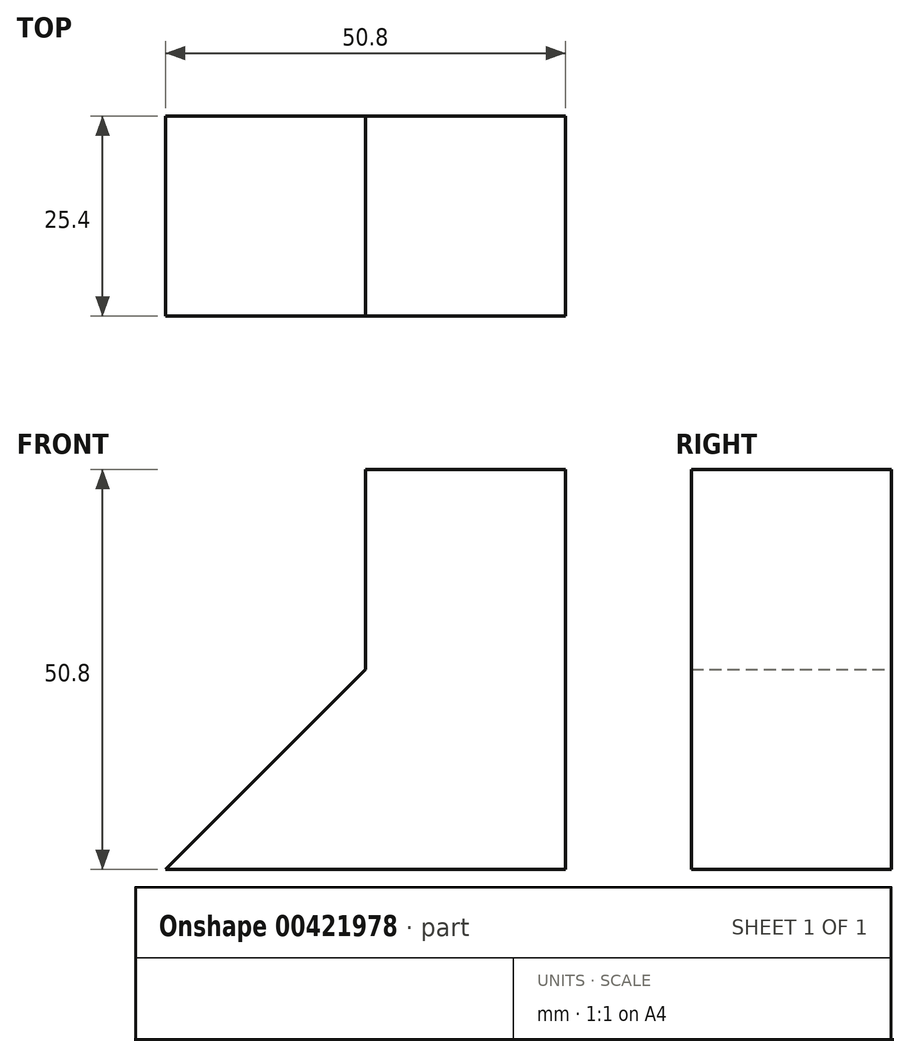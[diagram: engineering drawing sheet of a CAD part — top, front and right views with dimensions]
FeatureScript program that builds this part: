
annotation { "Feature Type Name" : "Feature", "Feature Type Description" : "" }
export const myFeature = defineFeature(function(context is Context, id is Id, definition is map)
    precondition{}
    {
        {
            var Q0;
            Q0=qCreatedBy(makeId("Front.planeOp"),FACE);
            var sketch = newSketch(context, id + "F0", { "sketchPlane" : qUnion([Q0])});
            skLineSegment(sketch, "E0", {"start": v(0, 0) * mm, "end": v(0, 50.8) * mm});
            skLineSegment(sketch, "E1", {"start": v(0, 50.8) * mm, "end": v(-25.4, 50.8) * mm});
            skLineSegment(sketch, "E2", {"start": v(-25.4, 50.8) * mm, "end": v(-25.4, 25.4) * mm});
            skLineSegment(sketch, "E3", {"start": v(0, 0) * mm, "end": v(-50.8, 0) * mm});
            skLineSegment(sketch, "E4", {"start": v(-25.4, 25.4) * mm, "end": v(-50.8, 0) * mm});
            skSolve(sketch);
        }
        {
            var Q0;
            Q0=makeQuery(id+"F0.imprint","IMPRINT",FACE,{"disambiguationData":[TD([[makeQuery(id+"F0.imprint","IMPRINT",EDGE,{"derivedFrom":sQuery(id+"F0.wireOp",EDGE,"E0")}),1.0]])]});
            extrude(context, id + "F1", {"entities" : qUnion([Q0]), "depth" : 25.4 * mm});
        }
    });
